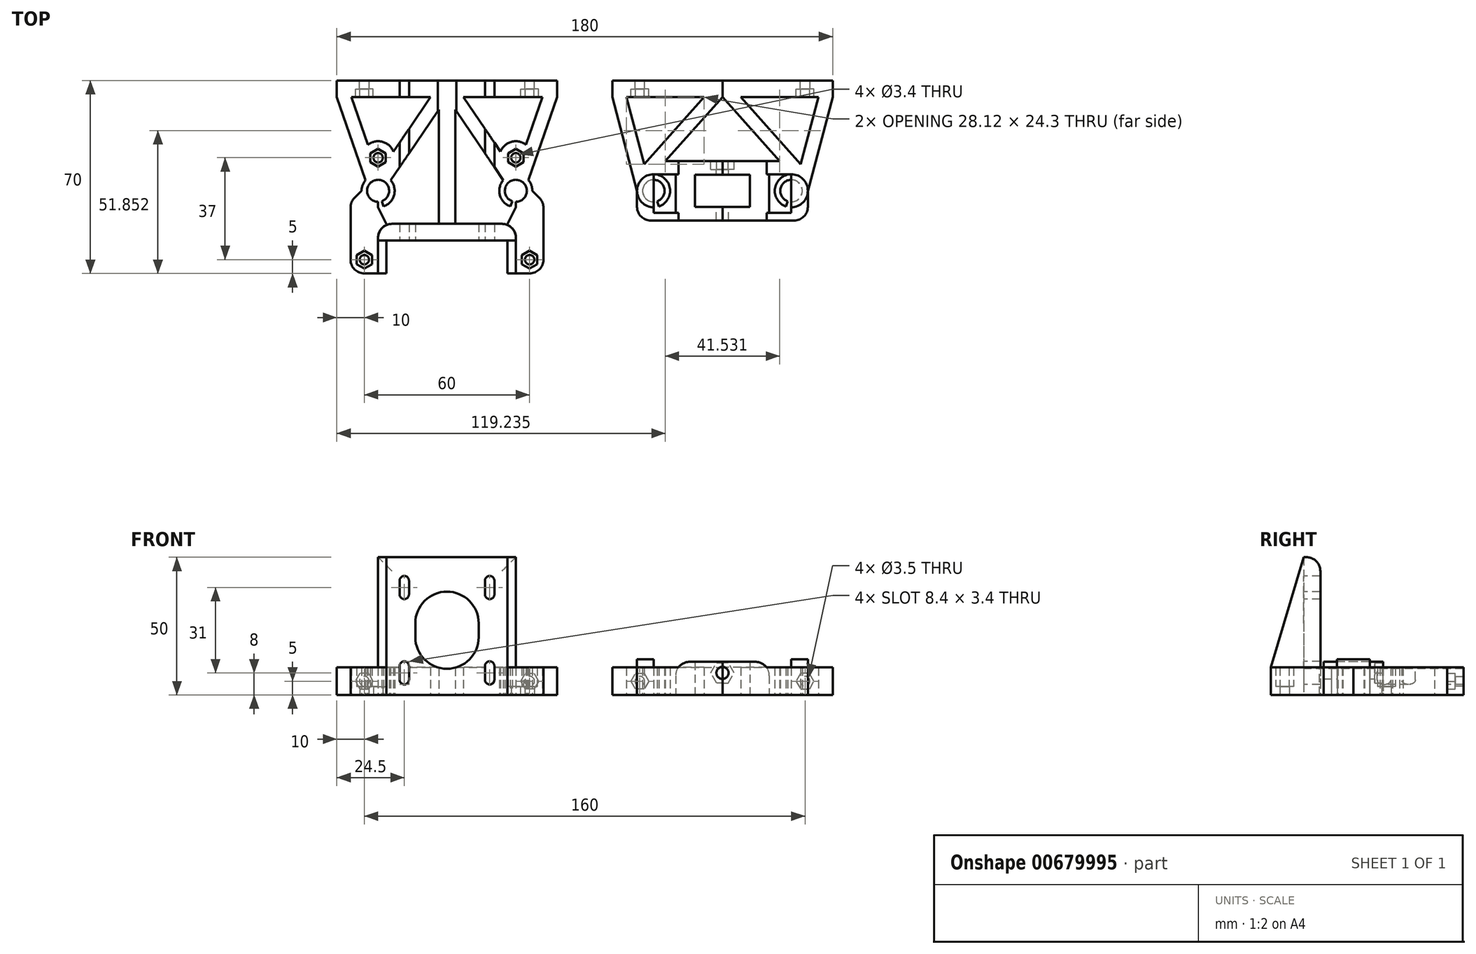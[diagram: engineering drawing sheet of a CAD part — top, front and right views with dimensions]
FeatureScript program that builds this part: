
annotation { "Feature Type Name" : "Feature", "Feature Type Description" : "" }
export const myFeature = defineFeature(function(context is Context, id is Id, definition is map)
    precondition{}
    {
        {
            var Q0;
            Q0=qCreatedBy(makeId("Top.planeOp"),FACE);
            var sketch = newSketch(context, id + "F0", { "sketchPlane" : qUnion([Q0])});
            skLineSegment(sketch, "E0", {"start": v(0, 0) * mm, "end": v(40, 0) * mm});
            skLineSegment(sketch, "E1", {"start": v(22, -58) * mm, "end": v(0, -58) * mm});
            skLineSegment(sketch, "E2", {"start": v(0, -58) * mm, "end": v(0, 0) * mm});
            skCircle(sketch, "E3", {"center": v(25, -40) * mm, "radius": 4 * mm});
            skLineSegment(sketch, "E4", {"start": v(22, -58) * mm, "end": v(22, -52) * mm});
            skLineSegment(sketch, "E5", {"start": v(22, -52) * mm, "end": v(0, -52) * mm});
            skCircle(sketch, "E6", {"center": v(25, -40) * mm, "radius": 6 * mm});
            skLineSegment(sketch, "E7", {"start": v(25, -40) * mm, "end": v(25, -46) * mm});
            skLineSegment(sketch, "E8", {"start": v(40, 0) * mm, "end": v(40, -6) * mm});
            skLineSegment(sketch, "E9", {"start": v(3, -10.48) * mm, "end": v(3, -52) * mm});
            skLineSegment(sketch, "E10", {"start": v(34.7, -6) * mm, "end": v(6, -6) * mm});
            skLineSegment(sketch, "E11", {"start": v(34.7, -6) * mm, "end": v(40, -6) * mm, "construction": true});
            skLineSegment(sketch, "E12", {"start": v(22, -52) * mm, "end": v(25, -46) * mm});
            skLineSegment(sketch, "E13", {"start": v(3, -10.48) * mm, "end": v(20.4, -36.14) * mm});
            skLineSegment(sketch, "E14", {"start": v(6, -6) * mm, "end": v(25, -34) * mm, "construction": true});
            skLineSegment(sketch, "E15", {"start": v(25, -34) * mm, "end": v(34.7, -6) * mm, "construction": true});
            skLineSegment(sketch, "E16", {"start": v(40, -6) * mm, "end": v(29.56, -36.1) * mm});
            skLineSegment(sketch, "E17", {"start": v(25, -40) * mm, "end": v(23, -45.66) * mm});
            skLineSegment(sketch, "E18", {"start": v(31, -40) * mm, "end": v(25, -40) * mm, "construction": true});
            skLineSegment(sketch, "E19", {"start": v(25, -40) * mm, "end": v(25, -34) * mm, "construction": true});
            skLineSegment(sketch, "E20", {"start": v(25, -34) * mm, "end": v(25, -28) * mm, "construction": true});
            skCircle(sketch, "E21", {"center": v(25, -28) * mm, "radius": 1.7 * mm});
            skArc(sketch, "E22", {"start": v(28.71, -23.29) * mm, "mid": v(23.44, -22.2) * mm, "end": v(19.42, -25.78) * mm});
            skLineSegment(sketch, "E23", {"start": v(28.71, -23.29) * mm, "end": v(34.7, -6) * mm});
            skLineSegment(sketch, "E24", {"start": v(19.42, -25.78) * mm, "end": v(6, -6) * mm});
            skCircle(sketch, "E25.cCircle", {"center": v(25, -28) * mm, "radius": 2.8 * mm, "construction": true});
            skLineSegment(sketch, "E25.0", {"start": v(27.8, -26.38) * mm, "end": v(27.8, -29.62) * mm});
            skLineSegment(sketch, "E25.1", {"start": v(27.8, -29.62) * mm, "end": v(25, -31.23) * mm});
            skLineSegment(sketch, "E25.2", {"start": v(25, -31.23) * mm, "end": v(22.2, -29.62) * mm});
            skLineSegment(sketch, "E25.3", {"start": v(22.2, -29.62) * mm, "end": v(22.2, -26.38) * mm});
            skLineSegment(sketch, "E25.4", {"start": v(22.2, -26.38) * mm, "end": v(25, -24.77) * mm});
            skLineSegment(sketch, "E25.5", {"start": v(25, -24.77) * mm, "end": v(27.8, -26.38) * mm});
            skPoint(sketch, "E25.0.midPoint", {"position": v(27.8, -28) * mm});
            skLineSegment(sketch, "E26", {"start": v(22, -58) * mm, "end": v(22, -70) * mm});
            skLineSegment(sketch, "E27", {"start": v(25, -46) * mm, "end": v(25, -70) * mm});
            skCircle(sketch, "E28", {"center": v(30, -65) * mm, "radius": 1.7 * mm});
            skCircle(sketch, "E29.cCircle", {"center": v(30, -65) * mm, "radius": 2.8 * mm, "construction": true});
            skLineSegment(sketch, "E29.0", {"start": v(32.8, -63.38) * mm, "end": v(32.8, -66.62) * mm});
            skLineSegment(sketch, "E29.1", {"start": v(32.8, -66.62) * mm, "end": v(30, -68.23) * mm});
            skLineSegment(sketch, "E29.2", {"start": v(30, -68.23) * mm, "end": v(27.2, -66.62) * mm});
            skLineSegment(sketch, "E29.3", {"start": v(27.2, -66.62) * mm, "end": v(27.2, -63.38) * mm});
            skLineSegment(sketch, "E29.4", {"start": v(27.2, -63.38) * mm, "end": v(30, -61.77) * mm});
            skLineSegment(sketch, "E29.5", {"start": v(30, -61.77) * mm, "end": v(32.8, -63.38) * mm});
            skPoint(sketch, "E29.0.midPoint", {"position": v(32.8, -65) * mm});
            skLineSegment(sketch, "E30", {"start": v(22, -70) * mm, "end": v(25, -70) * mm});
            skLineSegment(sketch, "E31", {"start": v(25, -70) * mm, "end": v(35, -70) * mm});
            skLineSegment(sketch, "E32", {"start": v(35, -70) * mm, "end": v(35, -44) * mm});
            skLineSegment(sketch, "E33", {"start": v(35, -44) * mm, "end": v(31, -40) * mm});
            skLineSegment(sketch, "E34", {"start": v(22, -52) * mm, "end": v(25, -52) * mm});
            skLineSegment(sketch, "E35", {"start": v(40, 0) * mm, "end": v(100, 0) * mm, "construction": true});
            skLineSegment(sketch, "E36", {"start": v(100, 0) * mm, "end": v(100, -6) * mm});
            skLineSegment(sketch, "E37", {"start": v(100, -6) * mm, "end": v(140, -6) * mm});
            skLineSegment(sketch, "E38", {"start": v(140, -6) * mm, "end": v(140, 0) * mm});
            skLineSegment(sketch, "E39", {"start": v(140, 0) * mm, "end": v(100, 0) * mm});
            skCircle(sketch, "E40", {"center": v(125, -40) * mm, "radius": 4 * mm});
            skCircle(sketch, "E41", {"center": v(125, -40) * mm, "radius": 6 * mm});
            skLineSegment(sketch, "E42", {"start": v(100, -6) * mm, "end": v(100, -56.52) * mm, "construction": true});
            skLineSegment(sketch, "E43", {"start": v(100, -34.2) * mm, "end": v(110, -34.2) * mm});
            skLineSegment(sketch, "E44", {"start": v(110, -34.2) * mm, "end": v(110, -45.8) * mm});
            skLineSegment(sketch, "E45", {"start": v(110, -45.8) * mm, "end": v(100, -45.8) * mm});
            skLineSegment(sketch, "E46", {"start": v(100, -45.8) * mm, "end": v(100, -50.8) * mm});
            skLineSegment(sketch, "E47", {"start": v(100, -50.8) * mm, "end": v(131, -50.8) * mm});
            skLineSegment(sketch, "E48", {"start": v(140, -6) * mm, "end": v(131, -40) * mm});
            skLineSegment(sketch, "E49", {"start": v(25, -40) * mm, "end": v(0, -40) * mm, "construction": true});
            skLineSegment(sketch, "E50", {"start": v(0, -40) * mm, "end": v(0, 0) * mm, "construction": true});
            skLineSegment(sketch, "E51", {"start": v(100, 0) * mm, "end": v(100, -40) * mm, "construction": true});
            skLineSegment(sketch, "E52", {"start": v(100, -40) * mm, "end": v(125, -40) * mm, "construction": true});
            skLineSegment(sketch, "E53", {"start": v(125, -40) * mm, "end": v(125, -46) * mm});
            skLineSegment(sketch, "E54", {"start": v(125, -40) * mm, "end": v(123, -45.66) * mm});
            skPoint(sketch, "E55", {"position": v(110, -40) * mm});
            skLineSegment(sketch, "E56", {"start": v(117, -48) * mm, "end": v(117, -34) * mm});
            skLineSegment(sketch, "E57", {"start": v(117, -34) * mm, "end": v(125, -34) * mm});
            skLineSegment(sketch, "E58", {"start": v(125, -34) * mm, "end": v(100, -6) * mm});
            skLineSegment(sketch, "E59", {"start": v(106.7, -6) * mm, "end": v(128.4, -30.3) * mm});
            skLineSegment(sketch, "E60", {"start": v(128.4, -30.3) * mm, "end": v(134.83, -6) * mm});
            skLineSegment(sketch, "E61", {"start": v(120.71, -29.2) * mm, "end": v(100, -29.2) * mm});
            skLineSegment(sketch, "E62", {"start": v(100, -29.2) * mm, "end": v(100, -34.2) * mm});
            skLineSegment(sketch, "E63", {"start": v(117, -48) * mm, "end": v(125, -48) * mm});
            skLineSegment(sketch, "E64", {"start": v(125, -48) * mm, "end": v(125, -46) * mm});
            skLineSegment(sketch, "E65", {"start": v(131, -50.8) * mm, "end": v(131, -40) * mm});
            skLineSegment(sketch, "E66", {"start": v(117, -34) * mm, "end": v(117, -29.2) * mm});
            skLineSegment(sketch, "E67", {"start": v(117, -48) * mm, "end": v(117, -50.8) * mm});
            skLineSegment(sketch, "E68", {"start": v(125, -40) * mm, "end": v(125, -34) * mm});
            skSolve(sketch);
        }
        {
            var Q0;
            {var subQ10=sQuery(id+"F0.wireOp",EDGE,"E0");Q0=makeQuery(id+"F0.imprint","IMPRINT",FACE,{"disambiguationData":[TD([[makeQuery(id+"F0.imprint","IMPRINT",EDGE,{"derivedFrom":subQ10}),-1.0]])]});}
            var Q1;
            {var subQ1=sQuery(id+"F0.wireOp",EDGE,"E3");var subQ6=sQuery(id+"F0.wireOp",EDGE,"E7");var subQ11=makeQuery(id+"F0.imprint","INTERSECT",VERTEX,{"derivedFrom":[subQ1,subQ6]});Q1=makeQuery(id+"F0.imprint","IMPRINT",FACE,{"disambiguationData":[TD([[makeQuery(id+"F0.imprint","IMPRINT",EDGE,{"disambiguationData":[TD([[subQ11,-1.0]])],"derivedFrom":subQ1}),-1.0]])]});}
            var Q2;
            Q2=makeQuery(id+"F0.imprint","IMPRINT",FACE,{"disambiguationData":[TD([[makeQuery(id+"F0.imprint","IMPRINT",EDGE,{"derivedFrom":sQuery(id+"F0.wireOp",EDGE,"E4")}),-1.0]])]});
            var Q3;
            {var subQ5=sQuery(id+"F0.wireOp",EDGE,"E1");Q3=makeQuery(id+"F0.imprint","IMPRINT",FACE,{"disambiguationData":[TD([[makeQuery(id+"F0.imprint","IMPRINT",EDGE,{"derivedFrom":subQ5}),-1.0]])]});}
            var Q4;
            {var subQ1=sQuery(id+"F0.wireOp",EDGE,"E27");Q4=makeQuery(id+"F0.imprint","IMPRINT",FACE,{"disambiguationData":[TD([[makeQuery(id+"F0.imprint","IMPRINT",EDGE,{"derivedFrom":subQ1}),1.0]])]});}
            var Q5;
            {var subQ2=sQuery(id+"F0.wireOp",EDGE,"E12");Q5=makeQuery(id+"F0.imprint","IMPRINT",FACE,{"disambiguationData":[TD([[makeQuery(id+"F0.imprint","IMPRINT",EDGE,{"derivedFrom":subQ2}),-1.0]])]});}
            extrude(context, id + "F1", {"entities" : qUnion([Q0, Q1, Q2, Q3, Q4, Q5]), "depth" : 10 * mm});
        }
        {
            var Q0;
            Q0=makeQuery(id+"F0.imprint","IMPRINT",FACE,{"disambiguationData":[TD([[makeQuery(id+"F0.imprint","IMPRINT",EDGE,{"derivedFrom":sQuery(id+"F0.wireOp",EDGE,"E21")}),-1.0]])]});
            var Q1;
            Q1=makeQuery(id+"F0.imprint","IMPRINT",FACE,{"disambiguationData":[TD([[makeQuery(id+"F0.imprint","IMPRINT",EDGE,{"derivedFrom":sQuery(id+"F0.wireOp",EDGE,"E28")}),-1.0]])]});
            extrude(context, id + "F2", {"entities" : qUnion([Q0, Q1]), "operationType" : NewBodyOperationType.ADD, "depth" : 3 * mm});
        }
        {
            var Q0;
            {var subQ6=sQuery(id+"F0.wireOp",EDGE,"E1");Q0=makeQuery(id+"F0.imprint","IMPRINT",FACE,{"disambiguationData":[TD([[makeQuery(id+"F0.imprint","IMPRINT",EDGE,{"derivedFrom":subQ6}),-1.0]])]});}
            var Q1;
            Q1=makeQuery(id+"F0.imprint","IMPRINT",FACE,{"disambiguationData":[TD([[makeQuery(id+"F0.imprint","IMPRINT",EDGE,{"derivedFrom":sQuery(id+"F0.wireOp",EDGE,"E4")}),-1.0]])]});
            extrude(context, id + "F3", {"entities" : qUnion([Q0, Q1]), "operationType" : NewBodyOperationType.ADD, "depth" : 50 * mm});
        }
        {
            var Q0;
            {var subQ0=sQuery(id+"F0.wireOp",EDGE,"E1");Q0=makeQuery(id+"F3.boolean.opBoolean","MERGE",FACE,{"derivedFrom":[makeQuery(id+"F1.opExtrude","SWEPT_FACE",FACE,{"disambiguationData":[OSD([subQ0,sQuery(id+"F0.wireOp",EDGE,"8d7ef4eb-627f-40db-80e5-a4429f437a70")])]}),makeQuery(id+"F3.opExtrude","SWEPT_FACE",FACE,{"disambiguationData":[OSD([subQ0])]})]});}
            var sketch = newSketch(context, id + "F4", { "sketchPlane" : qUnion([Q0])});
            skLineSegment(sketch, "E69", {"start": v(13.8, 10.5) * mm, "end": v(17.2, 10.5) * mm});
            skLineSegment(sketch, "E70", {"start": v(17.2, 10.5) * mm, "end": v(17.2, 5.5) * mm});
            skLineSegment(sketch, "E71", {"start": v(17.2, 5.5) * mm, "end": v(13.8, 5.5) * mm});
            skLineSegment(sketch, "E72", {"start": v(13.8, 5.5) * mm, "end": v(13.8, 10.5) * mm});
            skPoint(sketch, "E73", {"position": v(15.5, 10.5) * mm});
            skPoint(sketch, "E74", {"position": v(15.5, 5.5) * mm});
            skArc(sketch, "E75", {"start": v(17.2, 10.5) * mm, "mid": v(15.5, 12.2) * mm, "end": v(13.8, 10.5) * mm});
            skArc(sketch, "E76", {"start": v(13.8, 5.5) * mm, "mid": v(15.5, 3.8) * mm, "end": v(17.2, 5.5) * mm});
            skArc(sketch, "E77.0.1.0", {"start": v(13.8, 36.5) * mm, "mid": v(15.5, 34.8) * mm, "end": v(17.2, 36.5) * mm});
            skLineSegment(sketch, "E77.0.1.1", {"start": v(17.2, 41.5) * mm, "end": v(17.2, 36.5) * mm});
            skArc(sketch, "E77.0.1.2", {"start": v(17.2, 41.5) * mm, "mid": v(15.5, 43.2) * mm, "end": v(13.8, 41.5) * mm});
            skLineSegment(sketch, "E77.0.1.3", {"start": v(13.8, 36.5) * mm, "end": v(13.8, 41.5) * mm});
            skLineSegment(sketch, "E77.direction1", {"start": v(13.8, 5.5) * mm, "end": v(31.77, 5.5) * mm, "construction": true});
            skLineSegment(sketch, "E77.direction2", {"start": v(13.8, 5.5) * mm, "end": v(13.8, 36.5) * mm, "construction": true});
            skLineSegment(sketch, "E78", {"start": v(0, 0) * mm, "end": v(0, 26) * mm, "construction": true});
            skLineSegment(sketch, "E79", {"start": v(0, 26) * mm, "end": v(11.5, 26) * mm, "construction": true});
            skLineSegment(sketch, "E80", {"start": v(11.5, 26) * mm, "end": v(11.5, 21) * mm});
            skLineSegment(sketch, "E81", {"start": v(11.5, 21) * mm, "end": v(0, 21) * mm, "construction": true});
            skLineSegment(sketch, "E82.0.MirrorCS", {"start": v(-11.5, 26) * mm, "end": v(-11.5, 21) * mm});
            skArc(sketch, "E83", {"start": v(-11.5, 21) * mm, "mid": v(0, 9.5) * mm, "end": v(11.5, 21) * mm});
            skArc(sketch, "E84", {"start": v(11.5, 26) * mm, "mid": v(0, 37.5) * mm, "end": v(-11.5, 26) * mm});
            skSolve(sketch);
        }
        {
            var Q0;
            Q0=qSketchRegion(id+"F4",true);
            extrude(context, id + "F5", {"entities" : qUnion([Q0]), "operationType" : NewBodyOperationType.REMOVE, "endBound" : BoundingType.THROUGH_ALL, "oppositeDirection" : true, "depth" : 10 * mm});
        }
        {
            var Q0;
            Q0=makeQuery(id+"F3.opExtrude","SWEPT_FACE",FACE,{"disambiguationData":[OSD([sQuery(id+"F0.wireOp",EDGE,"E27")])]});
            var sketch = newSketch(context, id + "F6", { "sketchPlane" : qUnion([Q0])});
            skLineSegment(sketch, "E85", {"start": v(-58, 50) * mm, "end": v(-70, 50) * mm});
            skLineSegment(sketch, "E86", {"start": v(-70, 50) * mm, "end": v(-70, 10) * mm});
            skLineSegment(sketch, "E87", {"start": v(-70, 10) * mm, "end": v(-58, 50) * mm});
            skSolve(sketch);
        }
        {
            var Q0;
            Q0=makeQuery(id+"F6.imprint","IMPRINT",FACE,{"disambiguationData":[TD([[makeQuery(id+"F6.imprint","IMPRINT",EDGE,{"derivedFrom":sQuery(id+"F6.wireOp",EDGE,"E85")}),1.0]])]});
            extrude(context, id + "F7", {"entities" : qUnion([Q0]), "operationType" : NewBodyOperationType.REMOVE, "oppositeDirection" : true, "depth" : 5 * mm});
        }
        {
            var Q0;
            Q0=makeQuery(id+"F1.opExtrude","SWEPT_FACE",FACE,{"disambiguationData":[OSD([sQuery(id+"F0.wireOp",EDGE,"E0")])]});
            var sketch = newSketch(context, id + "F8", { "sketchPlane" : qUnion([Q0])});
            skCircle(sketch, "E88", {"center": v(-30, 5) * mm, "radius": 1.75 * mm});
            skCircle(sketch, "E89.cCircle", {"center": v(-30, 5) * mm, "radius": 2.8 * mm, "construction": true});
            skLineSegment(sketch, "E89.0", {"start": v(-31.62, 7.8) * mm, "end": v(-28.38, 7.8) * mm});
            skLineSegment(sketch, "E89.1", {"start": v(-28.38, 7.8) * mm, "end": v(-26.77, 5) * mm});
            skLineSegment(sketch, "E89.2", {"start": v(-26.77, 5) * mm, "end": v(-28.38, 2.2) * mm});
            skLineSegment(sketch, "E89.3", {"start": v(-28.38, 2.2) * mm, "end": v(-31.62, 2.2) * mm});
            skLineSegment(sketch, "E89.4", {"start": v(-31.62, 2.2) * mm, "end": v(-33.23, 5) * mm});
            skLineSegment(sketch, "E89.5", {"start": v(-33.23, 5) * mm, "end": v(-31.62, 7.8) * mm});
            skPoint(sketch, "E89.0.midPoint", {"position": v(-30, 7.8) * mm});
            skSolve(sketch);
        }
        {
            var Q0;
            Q0=makeQuery(id+"F8.imprint","IMPRINT",FACE,{"disambiguationData":[TD([[makeQuery(id+"F8.imprint","IMPRINT",EDGE,{"derivedFrom":sQuery(id+"F8.wireOp",EDGE,"E88")}),-1.0]])]});
            var Q1;
            Q1=makeQuery(id+"F8.imprint","IMPRINT",FACE,{"disambiguationData":[TD([[makeQuery(id+"F8.imprint","IMPRINT",EDGE,{"derivedFrom":sQuery(id+"F8.wireOp",EDGE,"E88")}),1.0]])]});
            extrude(context, id + "F9", {"entities" : qUnion([Q0, Q1]), "operationType" : NewBodyOperationType.REMOVE, "oppositeDirection" : true, "depth" : 8 * mm});
        }
        {
            var Q0;
            Q0=makeQuery(id+"F8.imprint","IMPRINT",FACE,{"disambiguationData":[TD([[makeQuery(id+"F8.imprint","IMPRINT",EDGE,{"derivedFrom":sQuery(id+"F8.wireOp",EDGE,"E88")}),-1.0]])]});
            extrude(context, id + "F10", {"entities" : qUnion([Q0]), "operationType" : NewBodyOperationType.ADD, "oppositeDirection" : true, "depth" : 3 * mm});
        }
        {
            var Q0;
            Q0=makeQuery(id+"F3.opExtrude","CAP_EDGE",EDGE,{"disambiguationData":[OSD([sQuery(id+"F0.wireOp",EDGE,"E5"),sQuery(id+"F0.wireOp",EDGE,"E34")])],"isStart":false});
            var Q1;
            Q1=makeQuery(id+"F3.opExtrude","SWEPT_EDGE",EDGE,{"disambiguationData":[OSD([sQuery(id+"F0.wireOp",EDGE,"E27"),sQuery(id+"F0.wireOp",EDGE,"E34")])]});
            var Q2;
            Q2=makeQuery(id+"F1.opExtrude","SWEPT_EDGE",EDGE,{"disambiguationData":[OSD([sQuery(id+"F0.wireOp",EDGE,"E32"),sQuery(id+"F0.wireOp",EDGE,"E33")])]});
            var Q3;
            Q3=makeQuery(id+"F1.opExtrude","SWEPT_EDGE",EDGE,{"disambiguationData":[OSD([sQuery(id+"F0.wireOp",EDGE,"E31"),sQuery(id+"F0.wireOp",EDGE,"E32")])]});
            var Q4;
            Q4=makeQuery(id+"F1.opExtrude","CAP_EDGE",EDGE,{"disambiguationData":[OSD([sQuery(id+"F0.wireOp",EDGE,"E9")])],"isStart":false});
            fillet(context, id + "F11", {"entities" : qUnion([Q0, Q1, Q2, Q3, Q4]), "radius" : 5 * mm, "tangentPropagation" : true, "allowEdgeOverflow" : false});
        }
        {
            var Q0;
            Q0=makeQuery(id+"F1.opExtrude","SWEPT_BODY",BODY,{"disambiguationData":[OSD([sQuery(id+"F0.wireOp",EDGE,"E0"),sQuery(id+"F0.wireOp",EDGE,"E2"),sQuery(id+"F0.wireOp",EDGE,"E3"),sQuery(id+"F0.wireOp",EDGE,"E5"),sQuery(id+"F0.wireOp",EDGE,"E6"),sQuery(id+"F0.wireOp",EDGE,"12cc076b-f364-463d-8a78-6dc26c333b14"),sQuery(id+"F0.wireOp",EDGE,"E7"),sQuery(id+"F0.wireOp",EDGE,"155325b8-6e32-41bb-954b-66700df3ed29"),sQuery(id+"F0.wireOp",EDGE,"E8"),sQuery(id+"F0.wireOp",EDGE,"7ea4bd2f-7135-466d-aa21-a694cee06c30"),sQuery(id+"F0.wireOp",EDGE,"E9"),sQuery(id+"F0.wireOp",EDGE,"db579d89-5200-47a7-b94c-b75dbc0a4807"),sQuery(id+"F0.wireOp",EDGE,"2259502c-a52b-4f63-be40-db7432d59570"),sQuery(id+"F0.wireOp",EDGE,"f2719385-8a71-408b-950c-d04906d04b55"),sQuery(id+"F0.wireOp",EDGE,"b7fa5365-783a-4351-8152-f1b30f844d2a"),sQuery(id+"F0.wireOp",EDGE,"E10")])]});
            var Q1;
            Q1=qCreatedBy(makeId("Right.planeOp"),FACE);
            mirror(context, id + "F12", {"operationType" : NewBodyOperationType.ADD, "entities" : qUnion([Q0]), "mirrorPlane" : qUnion([Q1])});
        }
        {
            var Q0;
            {var subQ0=sQuery(id+"F0.wireOp",EDGE,"E68");var subQ1=sQuery(id+"F0.wireOp",EDGE,"E40");var subQ2=makeQuery(id+"F0.imprint","INTERSECT",VERTEX,{"derivedFrom":[subQ1,subQ0]});Q0=makeQuery(id+"F0.imprint","IMPRINT",FACE,{"disambiguationData":[TD([[makeQuery(id+"F0.imprint","IMPRINT",EDGE,{"disambiguationData":[TD([[subQ2,1.0]])],"derivedFrom":subQ1}),-1.0]])]});}
            var Q1;
            {var subQ0=sQuery(id+"F0.wireOp",EDGE,"E68");var subQ1=sQuery(id+"F0.wireOp",EDGE,"E40");var subQ2=makeQuery(id+"F0.imprint","INTERSECT",VERTEX,{"derivedFrom":[subQ1,subQ0]});Q1=makeQuery(id+"F0.imprint","IMPRINT",FACE,{"disambiguationData":[TD([[makeQuery(id+"F0.imprint","IMPRINT",EDGE,{"disambiguationData":[TD([[subQ2,1.0]])],"derivedFrom":subQ1}),1.0]])]});}
            extrude(context, id + "F13", {"entities" : qUnion([Q0, Q1]), "depth" : 13 * mm});
        }
        {
            var Q0;
            {var subQ0=sQuery(id+"F0.wireOp",EDGE,"E68");var subQ1=sQuery(id+"F0.wireOp",EDGE,"E40");var subQ2=makeQuery(id+"F0.imprint","INTERSECT",VERTEX,{"derivedFrom":[subQ1,subQ0]});Q0=makeQuery(id+"F0.imprint","IMPRINT",FACE,{"disambiguationData":[TD([[makeQuery(id+"F0.imprint","IMPRINT",EDGE,{"disambiguationData":[TD([[subQ2,1.0]])],"derivedFrom":subQ1}),1.0]])]});}
            extrude(context, id + "F14", {"entities" : qUnion([Q0]), "operationType" : NewBodyOperationType.REMOVE, "depth" : 10 * mm});
        }
        {
            var Q0;
            {var subQ8=sQuery(id+"F0.wireOp",EDGE,"E48");Q0=makeQuery(id+"F0.imprint","IMPRINT",FACE,{"disambiguationData":[TD([[makeQuery(id+"F0.imprint","IMPRINT",EDGE,{"derivedFrom":subQ8}),-1.0]])]});}
            var Q1;
            {var subQ4=sQuery(id+"F0.wireOp",EDGE,"E57");Q1=makeQuery(id+"F0.imprint","IMPRINT",FACE,{"disambiguationData":[TD([[makeQuery(id+"F0.imprint","IMPRINT",EDGE,{"derivedFrom":subQ4}),1.0]])]});}
            var Q2;
            {var subQ1=sQuery(id+"F0.wireOp",EDGE,"E40");var subQ5=sQuery(id+"F0.wireOp",EDGE,"E54");var subQ6=makeQuery(id+"F0.imprint","INTERSECT",VERTEX,{"derivedFrom":[subQ1,subQ5]});Q2=makeQuery(id+"F0.imprint","IMPRINT",FACE,{"disambiguationData":[TD([[makeQuery(id+"F0.imprint","IMPRINT",EDGE,{"disambiguationData":[TD([[subQ6,1.0]])],"derivedFrom":subQ1}),-1.0]])]});}
            var Q3;
            Q3=makeQuery(id+"F0.imprint","IMPRINT",FACE,{"disambiguationData":[TD([[makeQuery(id+"F0.imprint","IMPRINT",EDGE,{"derivedFrom":sQuery(id+"F0.wireOp",EDGE,"E63")}),-1.0]])]});
            var Q4;
            {var subQ4=sQuery(id+"F0.wireOp",EDGE,"E36");Q4=makeQuery(id+"F0.imprint","IMPRINT",FACE,{"disambiguationData":[TD([[makeQuery(id+"F0.imprint","IMPRINT",EDGE,{"derivedFrom":subQ4}),1.0]])]});}
            extrude(context, id + "F15", {"entities" : qUnion([Q0, Q1, Q2, Q3, Q4]), "operationType" : NewBodyOperationType.ADD, "depth" : 10 * mm});
        }
        {
            var Q0;
            Q0=makeQuery(id+"F0.imprint","IMPRINT",FACE,{"disambiguationData":[TD([[makeQuery(id+"F0.imprint","IMPRINT",EDGE,{"derivedFrom":sQuery(id+"F0.wireOp",EDGE,"E43")}),1.0]])]});
            extrude(context, id + "F16", {"entities" : qUnion([Q0]), "operationType" : NewBodyOperationType.ADD, "depth" : 12 * mm});
        }
        {
            var Q0;
            {var subQ0=sQuery(id+"F0.wireOp",EDGE,"E61");Q0=makeQuery(id+"F16.boolean.opBoolean","MERGE",FACE,{"derivedFrom":[makeQuery(id+"F15.opExtrude","SWEPT_FACE",FACE,{"disambiguationData":[OSD([subQ0])]}),makeQuery(id+"F16.opExtrude","SWEPT_FACE",FACE,{"disambiguationData":[OSD([subQ0])]})]});}
            var sketch = newSketch(context, id + "F17", { "sketchPlane" : qUnion([Q0])});
            skCircle(sketch, "E90", {"center": v(-100, 8) * mm, "radius": 2.2 * mm});
            skCircle(sketch, "E91.cCircle", {"center": v(-100, 8) * mm, "radius": 3.65 * mm, "construction": true});
            skLineSegment(sketch, "E91.0", {"start": v(-102.1, 11.65) * mm, "end": v(-97.9, 11.65) * mm});
            skLineSegment(sketch, "E91.1", {"start": v(-97.9, 11.65) * mm, "end": v(-95.79, 8) * mm});
            skLineSegment(sketch, "E91.2", {"start": v(-95.79, 8) * mm, "end": v(-97.9, 4.35) * mm});
            skLineSegment(sketch, "E91.3", {"start": v(-97.9, 4.35) * mm, "end": v(-102.1, 4.35) * mm});
            skLineSegment(sketch, "E91.4", {"start": v(-102.1, 4.35) * mm, "end": v(-104.21, 8) * mm});
            skLineSegment(sketch, "E91.5", {"start": v(-104.21, 8) * mm, "end": v(-102.1, 11.65) * mm});
            skPoint(sketch, "E91.0.midPoint", {"position": v(-100, 11.65) * mm});
            skSolve(sketch);
        }
        {
            var Q0;
            {var subQ0=makeQuery(id+"F16.opExtrude","SWEPT_EDGE",EDGE,{"disambiguationData":[OSD([sQuery(id+"F0.wireOp",EDGE,"E61"),sQuery(id+"F0.wireOp",EDGE,"E62")])]});var subQ1=sQuery(id+"F17.wireOp",EDGE,"E90");var subQ3=makeQuery(id+"F17.imprint","INTERSECT",VERTEX,{"disambiguationData":[OD(0.0)],"derivedFrom":[subQ0,subQ1]});Q0=makeQuery(id+"F17.imprint","IMPRINT",FACE,{"disambiguationData":[TD([[makeQuery(id+"F17.imprint","IMPRINT",EDGE,{"disambiguationData":[TD([[subQ3,-1.0]])],"derivedFrom":subQ1}),1.0]])]});}
            extrude(context, id + "F18", {"entities" : qUnion([Q0]), "operationType" : NewBodyOperationType.REMOVE, "endBound" : BoundingType.THROUGH_ALL, "oppositeDirection" : true, "depth" : 25 * mm});
        }
        {
            var Q0;
            {var subQ9=sQuery(id+"F17.wireOp",EDGE,"E91.4");Q0=makeQuery(id+"F17.imprint","IMPRINT",FACE,{"disambiguationData":[TD([[makeQuery(id+"F17.imprint","IMPRINT",EDGE,{"derivedFrom":subQ9}),-1.0]])]});}
            extrude(context, id + "F19", {"entities" : qUnion([Q0]), "operationType" : NewBodyOperationType.REMOVE, "oppositeDirection" : true, "depth" : 3 * mm});
        }
        {
            var Q0;
            Q0=makeQuery(id+"F15.opExtrude","SWEPT_FACE",FACE,{"disambiguationData":[OSD([sQuery(id+"F0.wireOp",EDGE,"E39")])]});
            var sketch = newSketch(context, id + "F20", { "sketchPlane" : qUnion([Q0])});
            skCircle(sketch, "E92", {"center": v(-130, 5) * mm, "radius": 1.75 * mm});
            skCircle(sketch, "E93.cCircle", {"center": v(-130, 5) * mm, "radius": 2.8 * mm, "construction": true});
            skLineSegment(sketch, "E93.0", {"start": v(-131.62, 7.8) * mm, "end": v(-128.38, 7.8) * mm});
            skLineSegment(sketch, "E93.1", {"start": v(-128.38, 7.8) * mm, "end": v(-126.77, 5) * mm});
            skLineSegment(sketch, "E93.2", {"start": v(-126.77, 5) * mm, "end": v(-128.38, 2.2) * mm});
            skLineSegment(sketch, "E93.3", {"start": v(-128.38, 2.2) * mm, "end": v(-131.62, 2.2) * mm});
            skLineSegment(sketch, "E93.4", {"start": v(-131.62, 2.2) * mm, "end": v(-133.23, 5) * mm});
            skLineSegment(sketch, "E93.5", {"start": v(-133.23, 5) * mm, "end": v(-131.62, 7.8) * mm});
            skPoint(sketch, "E93.0.midPoint", {"position": v(-130, 7.8) * mm});
            skSolve(sketch);
        }
        {
            var Q0;
            Q0=makeQuery(id+"F20.imprint","IMPRINT",FACE,{"disambiguationData":[TD([[makeQuery(id+"F20.imprint","IMPRINT",EDGE,{"derivedFrom":sQuery(id+"F20.wireOp",EDGE,"E92")}),-1.0]])]});
            var Q1;
            Q1=makeQuery(id+"F20.imprint","IMPRINT",FACE,{"disambiguationData":[TD([[makeQuery(id+"F20.imprint","IMPRINT",EDGE,{"derivedFrom":sQuery(id+"F20.wireOp",EDGE,"E92")}),1.0]])]});
            extrude(context, id + "F21", {"entities" : qUnion([Q0, Q1]), "operationType" : NewBodyOperationType.REMOVE, "oppositeDirection" : true, "depth" : 10 * mm});
        }
        {
            var Q0;
            Q0=makeQuery(id+"F20.imprint","IMPRINT",FACE,{"disambiguationData":[TD([[makeQuery(id+"F20.imprint","IMPRINT",EDGE,{"derivedFrom":sQuery(id+"F20.wireOp",EDGE,"E92")}),-1.0]])]});
            extrude(context, id + "F22", {"entities" : qUnion([Q0]), "operationType" : NewBodyOperationType.ADD, "oppositeDirection" : true, "depth" : 3 * mm});
        }
        {
            var Q0;
            Q0=makeQuery(id+"F15.opExtrude","SWEPT_EDGE",EDGE,{"disambiguationData":[OSD([sQuery(id+"F0.wireOp",EDGE,"E47"),sQuery(id+"F0.wireOp",EDGE,"E65")])]});
            var Q1;
            Q1=makeQuery(id+"F16.opExtrude","CAP_EDGE",EDGE,{"disambiguationData":[OSD([sQuery(id+"F0.wireOp",EDGE,"E56"),sQuery(id+"F0.wireOp",EDGE,"E66"),sQuery(id+"F0.wireOp",EDGE,"E67")])],"isStart":false});
            fillet(context, id + "F23", {"entities" : qUnion([Q0, Q1]), "radius" : 5 * mm, "tangentPropagation" : true, "allowEdgeOverflow" : false});
        }
        {
            var Q0;
            Q0=makeQuery(id+"F13.opExtrude","SWEPT_BODY",BODY,{"disambiguationData":[OSD([sQuery(id+"F0.wireOp",EDGE,"E41"),sQuery(id+"F0.wireOp",EDGE,"E53"),sQuery(id+"F0.wireOp",EDGE,"E68")])]});
            var Q1;
            Q1=makeQuery(id+"F15.opExtrude","SWEPT_FACE",FACE,{"disambiguationData":[OSD([sQuery(id+"F0.wireOp",EDGE,"E36")])]});
            mirror(context, id + "F24", {"operationType" : NewBodyOperationType.ADD, "entities" : qUnion([Q0]), "mirrorPlane" : qUnion([Q1])});
        }
    });
